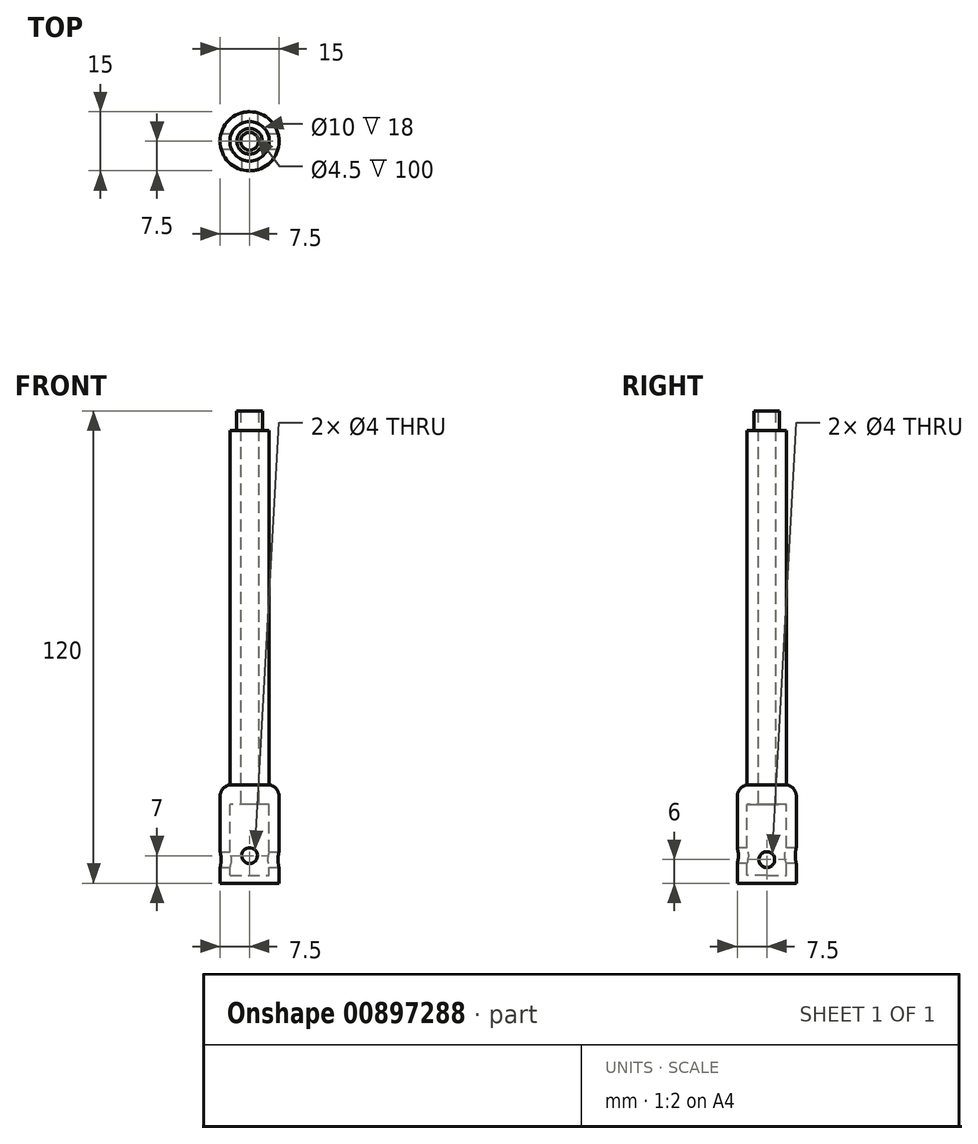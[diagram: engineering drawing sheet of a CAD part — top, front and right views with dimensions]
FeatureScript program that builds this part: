
annotation { "Feature Type Name" : "Feature", "Feature Type Description" : "" }
export const myFeature = defineFeature(function(context is Context, id is Id, definition is map)
    precondition{}
    {
        {
            var Q0;
            Q0=qCreatedBy(makeId("Top.planeOp"),FACE);
            var sketch = newSketch(context, id + "F0", { "sketchPlane" : qUnion([Q0])});
            skCircle(sketch, "E0", {"center": v(0, 0) * mm, "radius": 2.25 * mm});
            skCircle(sketch, "E1", {"center": v(0, 0) * mm, "radius": 3.25 * mm});
            skCircle(sketch, "E2", {"center": v(0, 0) * mm, "radius": 5 * mm});
            skCircle(sketch, "E3", {"center": v(0, 0) * mm, "radius": 7.5 * mm});
            skSolve(sketch);
        }
        {
            var Q0;
            Q0=makeQuery(id+"F0.imprint","IMPRINT",FACE,{"disambiguationData":[TD([[makeQuery(id+"F0.imprint","IMPRINT",EDGE,{"derivedFrom":sQuery(id+"F0.wireOp",EDGE,"E0")}),-1.0]])]});
            extrude(context, id + "F1", {"entities" : qUnion([Q0]), "depth" : 100 * mm, "offsetDistance" : 25 * mm});
        }
        {
            var Q0;
            Q0=makeQuery(id+"F0.imprint","IMPRINT",FACE,{"disambiguationData":[TD([[makeQuery(id+"F0.imprint","IMPRINT",EDGE,{"derivedFrom":sQuery(id+"F0.wireOp",EDGE,"E1")}),-1.0]])]});
            extrude(context, id + "F2", {"entities" : qUnion([Q0]), "operationType" : NewBodyOperationType.ADD, "depth" : 95 * mm, "offsetDistance" : 25 * mm});
        }
        {
            var Q0;
            Q0=makeQuery(id+"F0.imprint","IMPRINT",FACE,{"disambiguationData":[TD([[makeQuery(id+"F0.imprint","IMPRINT",EDGE,{"derivedFrom":sQuery(id+"F0.wireOp",EDGE,"E2")}),-1.0]])]});
            extrude(context, id + "F3", {"entities" : qUnion([Q0]), "operationType" : NewBodyOperationType.ADD, "depth" : 5 * mm, "offsetDistance" : 25 * mm});
        }
        {
            var Q0;
            Q0=makeQuery(id+"F0.imprint","IMPRINT",FACE,{"disambiguationData":[TD([[makeQuery(id+"F0.imprint","IMPRINT",EDGE,{"derivedFrom":sQuery(id+"F0.wireOp",EDGE,"E2")}),-1.0]])]});
            extrude(context, id + "F4", {"entities" : qUnion([Q0]), "operationType" : NewBodyOperationType.ADD, "oppositeDirection" : true, "depth" : 20 * mm, "offsetDistance" : 25 * mm});
        }
        {
            var Q0;
            Q0=makeQuery(id+"F4.opExtrude","CAP_FACE",FACE,{"disambiguationData":[OSD([sQuery(id+"F0.wireOp",EDGE,"E2"),sQuery(id+"F0.wireOp",EDGE,"E3")])],"isStart":false});
            cPlane(context, id + "F5", {"entities" : qUnion([Q0]), "cplaneType" : CPlaneType.OFFSET, "offset" : 0 * mm, "width" : 150 * mm, "height" : 150 * mm});
        }
        {
            var Q0;
            Q0=qCreatedBy(id+"F5.planeOp",FACE);
            var sketch = newSketch(context, id + "F6", { "sketchPlane" : qUnion([Q0])});
            skCircle(sketch, "E4", {"center": v(0, 0) * mm, "radius": 5.5 * mm});
            skSolve(sketch);
        }
        {
            var Q0;
            Q0 = qSketchRegion(id + "F6", true);
            extrude(context, id + "F7", {"entities" : qUnion([Q0]), "operationType" : NewBodyOperationType.ADD, "oppositeDirection" : true, "depth" : 2 * mm, "offsetDistance" : 25 * mm});
        }
        {
            var Q0;
            Q0=qCreatedBy(makeId("Front.planeOp"),FACE);
            var sketch = newSketch(context, id + "F8", { "sketchPlane" : qUnion([Q0])});
            skCircle(sketch, "E5", {"center": v(0, -13) * mm, "radius": 2 * mm});
            skSolve(sketch);
        }
        {
            var Q0;
            Q0 = qSketchRegion(id + "F8", true);
            extrude(context, id + "F9", {"entities" : qUnion([Q0]), "operationType" : NewBodyOperationType.REMOVE, "endBound" : BoundingType.SYMMETRIC, "oppositeDirection" : true, "depth" : 25 * mm, "offsetDistance" : 25 * mm});
        }
        {
            var Q0;
            Q0=qCreatedBy(makeId("Right.planeOp"),FACE);
            var sketch = newSketch(context, id + "F10", { "sketchPlane" : qUnion([Q0])});
            skCircle(sketch, "E6", {"center": v(0, -14) * mm, "radius": 2 * mm});
            skSolve(sketch);
        }
        {
            var Q0;
            Q0 = qSketchRegion(id + "F10", true);
            extrude(context, id + "F11", {"entities" : qUnion([Q0]), "operationType" : NewBodyOperationType.REMOVE, "endBound" : BoundingType.SYMMETRIC, "oppositeDirection" : true, "depth" : 25 * mm, "offsetDistance" : 25 * mm});
        }
        {
            var Q0;
            Q0=makeQuery(id+"F3.opExtrude","CAP_EDGE",EDGE,{"disambiguationData":[OSD([sQuery(id+"F0.wireOp",EDGE,"E3")])],"isStart":false});
            fillet(context, id + "F12", {"entities" : qUnion([Q0]), "radius" : 3 * mm, "tangentPropagation" : true, "allowEdgeOverflow" : false});
        }
    });
